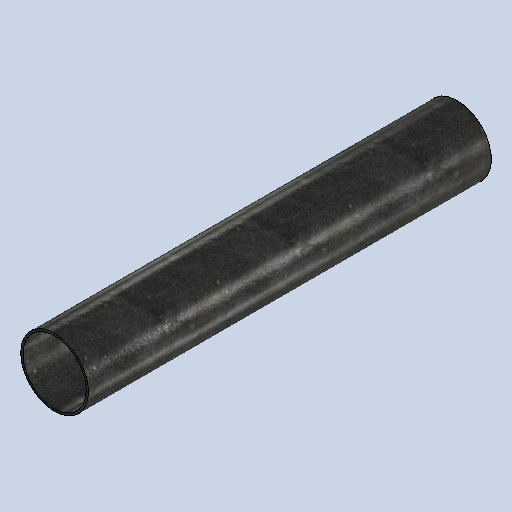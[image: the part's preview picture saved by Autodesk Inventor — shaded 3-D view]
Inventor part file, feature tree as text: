
AUTODESK INVENTOR PART (.ipt)
format: ipt  version: 2025.1 (Build 291241020, 241B)  size: 183,808 bytes
history: native  units: mm
features: extrude x1, sketch x1
ambient origin geometry x8: Origin, YZ Plane, XZ Plane, XY Plane, X Axis, Y Axis, Z Axis, Center Point
bodies: Solid1 (feature_tree)
feature tree (2):
  extrude  "Extrusion1"  Depth=535.0mm
  sketch  "Sketch1"  dims[d0=90.0mm d1=3.0mm d2=535.0mm d3=0.0mm]
